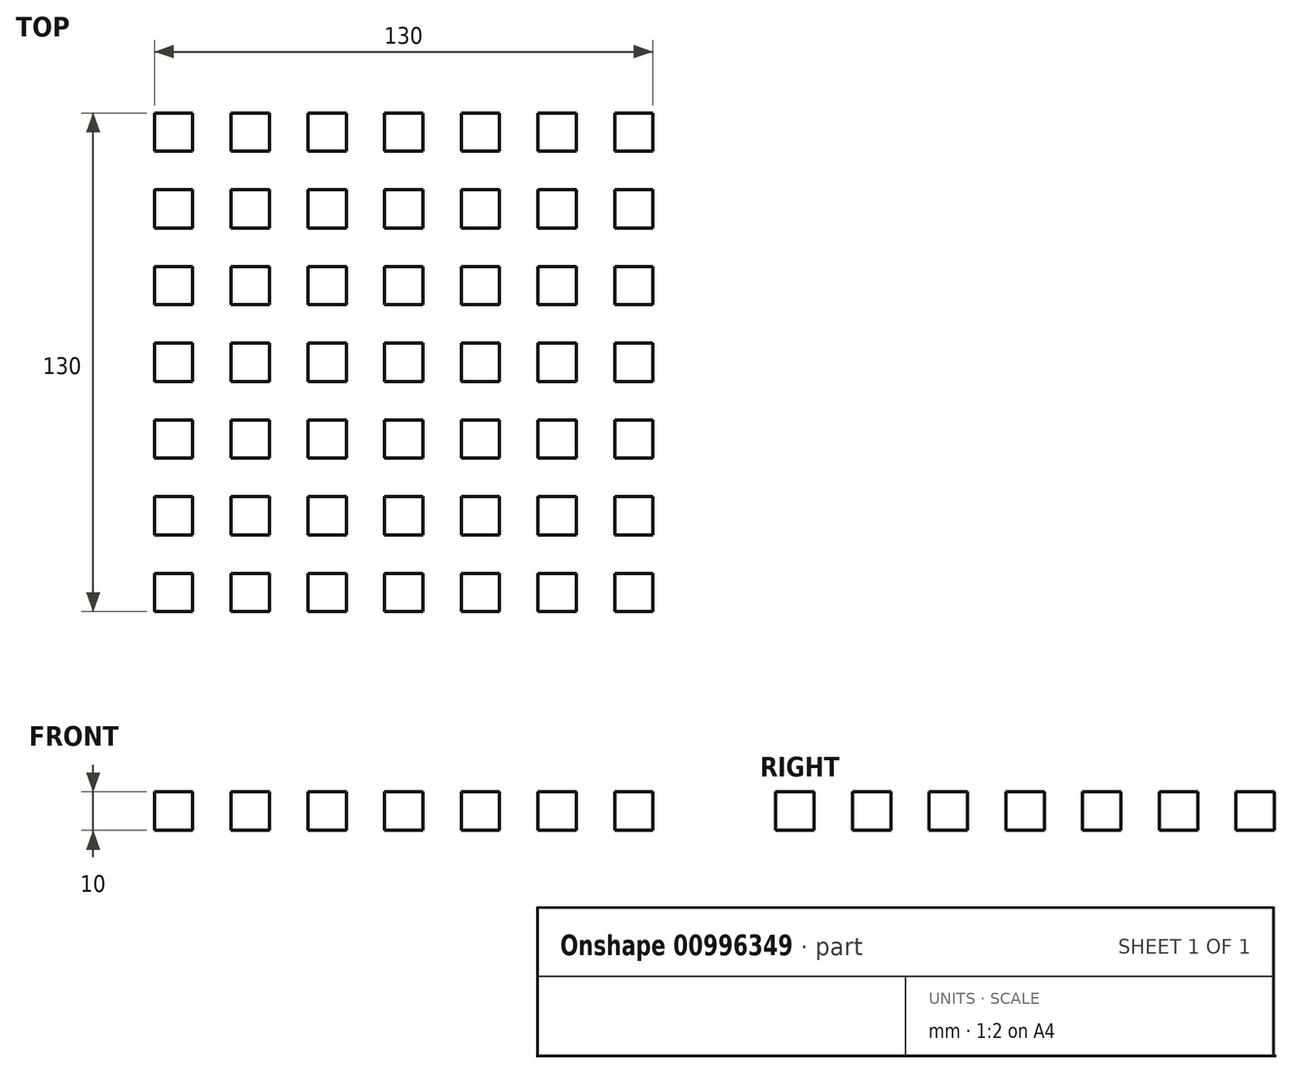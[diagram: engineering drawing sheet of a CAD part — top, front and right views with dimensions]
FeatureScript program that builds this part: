
annotation { "Feature Type Name" : "Feature", "Feature Type Description" : "" }
export const myFeature = defineFeature(function(context is Context, id is Id, definition is map)
    precondition{}
    {
        {
            var Q0;
            Q0=qCreatedBy(makeId("Top.planeOp"),FACE);
            var sketch = newSketch(context, id + "F0", { "sketchPlane" : qUnion([Q0])});
            skLineSegment(sketch, "E0.bottom", {"start": v(-62.96, -56.12) * mm, "end": v(-52.96, -56.12) * mm});
            skLineSegment(sketch, "E0.top", {"start": v(-62.96, -66.12) * mm, "end": v(-52.96, -66.12) * mm});
            skLineSegment(sketch, "E0.left", {"start": v(-62.96, -56.12) * mm, "end": v(-62.96, -66.12) * mm});
            skLineSegment(sketch, "E0.right", {"start": v(-52.96, -56.12) * mm, "end": v(-52.96, -66.12) * mm});
            skLineSegment(sketch, "E1.0.1.0", {"start": v(-62.96, -36.12) * mm, "end": v(-62.96, -46.12) * mm});
            skLineSegment(sketch, "E1.0.1.1", {"start": v(-52.96, -36.12) * mm, "end": v(-52.96, -46.12) * mm});
            skLineSegment(sketch, "E1.0.1.2", {"start": v(-62.96, -36.12) * mm, "end": v(-52.96, -36.12) * mm});
            skLineSegment(sketch, "E1.0.1.3", {"start": v(-62.96, -46.12) * mm, "end": v(-52.96, -46.12) * mm});
            skLineSegment(sketch, "E1.0.2.0", {"start": v(-62.96, -16.12) * mm, "end": v(-62.96, -26.12) * mm});
            skLineSegment(sketch, "E1.0.2.1", {"start": v(-52.96, -16.12) * mm, "end": v(-52.96, -26.12) * mm});
            skLineSegment(sketch, "E1.0.2.2", {"start": v(-62.96, -16.12) * mm, "end": v(-52.96, -16.12) * mm});
            skLineSegment(sketch, "E1.0.2.3", {"start": v(-62.96, -26.12) * mm, "end": v(-52.96, -26.12) * mm});
            skLineSegment(sketch, "E1.0.3.0", {"start": v(-62.96, 3.88) * mm, "end": v(-62.96, -6.12) * mm});
            skLineSegment(sketch, "E1.0.3.1", {"start": v(-52.96, 3.88) * mm, "end": v(-52.96, -6.12) * mm});
            skLineSegment(sketch, "E1.0.3.2", {"start": v(-62.96, 3.88) * mm, "end": v(-52.96, 3.88) * mm});
            skLineSegment(sketch, "E1.0.3.3", {"start": v(-62.96, -6.12) * mm, "end": v(-52.96, -6.12) * mm});
            skLineSegment(sketch, "E1.0.4.0", {"start": v(-62.96, 23.88) * mm, "end": v(-62.96, 13.88) * mm});
            skLineSegment(sketch, "E1.0.4.1", {"start": v(-52.96, 23.88) * mm, "end": v(-52.96, 13.88) * mm});
            skLineSegment(sketch, "E1.0.4.2", {"start": v(-62.96, 23.88) * mm, "end": v(-52.96, 23.88) * mm});
            skLineSegment(sketch, "E1.0.4.3", {"start": v(-62.96, 13.88) * mm, "end": v(-52.96, 13.88) * mm});
            skLineSegment(sketch, "E1.1.0.0", {"start": v(-42.96, -56.12) * mm, "end": v(-42.96, -66.12) * mm});
            skLineSegment(sketch, "E1.1.0.1", {"start": v(-32.96, -56.12) * mm, "end": v(-32.96, -66.12) * mm});
            skLineSegment(sketch, "E1.1.0.2", {"start": v(-42.96, -56.12) * mm, "end": v(-32.96, -56.12) * mm});
            skLineSegment(sketch, "E1.1.0.3", {"start": v(-42.96, -66.12) * mm, "end": v(-32.96, -66.12) * mm});
            skLineSegment(sketch, "E1.1.1.0", {"start": v(-42.96, -36.12) * mm, "end": v(-42.96, -46.12) * mm});
            skLineSegment(sketch, "E1.1.1.1", {"start": v(-32.96, -36.12) * mm, "end": v(-32.96, -46.12) * mm});
            skLineSegment(sketch, "E1.1.1.2", {"start": v(-42.96, -36.12) * mm, "end": v(-32.96, -36.12) * mm});
            skLineSegment(sketch, "E1.1.1.3", {"start": v(-42.96, -46.12) * mm, "end": v(-32.96, -46.12) * mm});
            skLineSegment(sketch, "E1.1.2.0", {"start": v(-42.96, -16.12) * mm, "end": v(-42.96, -26.12) * mm});
            skLineSegment(sketch, "E1.1.2.1", {"start": v(-32.96, -16.12) * mm, "end": v(-32.96, -26.12) * mm});
            skLineSegment(sketch, "E1.1.2.2", {"start": v(-42.96, -16.12) * mm, "end": v(-32.96, -16.12) * mm});
            skLineSegment(sketch, "E1.1.2.3", {"start": v(-42.96, -26.12) * mm, "end": v(-32.96, -26.12) * mm});
            skLineSegment(sketch, "E1.1.3.0", {"start": v(-42.96, 3.88) * mm, "end": v(-42.96, -6.12) * mm});
            skLineSegment(sketch, "E1.1.3.1", {"start": v(-32.96, 3.88) * mm, "end": v(-32.96, -6.12) * mm});
            skLineSegment(sketch, "E1.1.3.2", {"start": v(-42.96, 3.88) * mm, "end": v(-32.96, 3.88) * mm});
            skLineSegment(sketch, "E1.1.3.3", {"start": v(-42.96, -6.12) * mm, "end": v(-32.96, -6.12) * mm});
            skLineSegment(sketch, "E1.1.4.0", {"start": v(-42.96, 23.88) * mm, "end": v(-42.96, 13.88) * mm});
            skLineSegment(sketch, "E1.1.4.1", {"start": v(-32.96, 23.88) * mm, "end": v(-32.96, 13.88) * mm});
            skLineSegment(sketch, "E1.1.4.2", {"start": v(-42.96, 23.88) * mm, "end": v(-32.96, 23.88) * mm});
            skLineSegment(sketch, "E1.1.4.3", {"start": v(-42.96, 13.88) * mm, "end": v(-32.96, 13.88) * mm});
            skLineSegment(sketch, "E1.2.0.0", {"start": v(-22.96, -56.12) * mm, "end": v(-22.96, -66.12) * mm});
            skLineSegment(sketch, "E1.2.0.1", {"start": v(-12.96, -56.12) * mm, "end": v(-12.96, -66.12) * mm});
            skLineSegment(sketch, "E1.2.0.2", {"start": v(-22.96, -56.12) * mm, "end": v(-12.96, -56.12) * mm});
            skLineSegment(sketch, "E1.2.0.3", {"start": v(-22.96, -66.12) * mm, "end": v(-12.96, -66.12) * mm});
            skLineSegment(sketch, "E1.2.1.0", {"start": v(-22.96, -36.12) * mm, "end": v(-22.96, -46.12) * mm});
            skLineSegment(sketch, "E1.2.1.1", {"start": v(-12.96, -36.12) * mm, "end": v(-12.96, -46.12) * mm});
            skLineSegment(sketch, "E1.2.1.2", {"start": v(-22.96, -36.12) * mm, "end": v(-12.96, -36.12) * mm});
            skLineSegment(sketch, "E1.2.1.3", {"start": v(-22.96, -46.12) * mm, "end": v(-12.96, -46.12) * mm});
            skLineSegment(sketch, "E1.2.2.0", {"start": v(-22.96, -16.12) * mm, "end": v(-22.96, -26.12) * mm});
            skLineSegment(sketch, "E1.2.2.1", {"start": v(-12.96, -16.12) * mm, "end": v(-12.96, -26.12) * mm});
            skLineSegment(sketch, "E1.2.2.2", {"start": v(-22.96, -16.12) * mm, "end": v(-12.96, -16.12) * mm});
            skLineSegment(sketch, "E1.2.2.3", {"start": v(-22.96, -26.12) * mm, "end": v(-12.96, -26.12) * mm});
            skLineSegment(sketch, "E1.2.3.0", {"start": v(-22.96, 3.88) * mm, "end": v(-22.96, -6.12) * mm});
            skLineSegment(sketch, "E1.2.3.1", {"start": v(-12.96, 3.88) * mm, "end": v(-12.96, -6.12) * mm});
            skLineSegment(sketch, "E1.2.3.2", {"start": v(-22.96, 3.88) * mm, "end": v(-12.96, 3.88) * mm});
            skLineSegment(sketch, "E1.2.3.3", {"start": v(-22.96, -6.12) * mm, "end": v(-12.96, -6.12) * mm});
            skLineSegment(sketch, "E1.2.4.0", {"start": v(-22.96, 23.88) * mm, "end": v(-22.96, 13.88) * mm});
            skLineSegment(sketch, "E1.2.4.1", {"start": v(-12.96, 23.88) * mm, "end": v(-12.96, 13.88) * mm});
            skLineSegment(sketch, "E1.2.4.2", {"start": v(-22.96, 23.88) * mm, "end": v(-12.96, 23.88) * mm});
            skLineSegment(sketch, "E1.2.4.3", {"start": v(-22.96, 13.88) * mm, "end": v(-12.96, 13.88) * mm});
            skLineSegment(sketch, "E1.3.0.0", {"start": v(-2.96, -56.12) * mm, "end": v(-2.96, -66.12) * mm});
            skLineSegment(sketch, "E1.3.0.1", {"start": v(7.04, -56.12) * mm, "end": v(7.04, -66.12) * mm});
            skLineSegment(sketch, "E1.3.0.2", {"start": v(-2.96, -56.12) * mm, "end": v(7.04, -56.12) * mm});
            skLineSegment(sketch, "E1.3.0.3", {"start": v(-2.96, -66.12) * mm, "end": v(7.04, -66.12) * mm});
            skLineSegment(sketch, "E1.3.1.0", {"start": v(-2.96, -36.12) * mm, "end": v(-2.96, -46.12) * mm});
            skLineSegment(sketch, "E1.3.1.1", {"start": v(7.04, -36.12) * mm, "end": v(7.04, -46.12) * mm});
            skLineSegment(sketch, "E1.3.1.2", {"start": v(-2.96, -36.12) * mm, "end": v(7.04, -36.12) * mm});
            skLineSegment(sketch, "E1.3.1.3", {"start": v(-2.96, -46.12) * mm, "end": v(7.04, -46.12) * mm});
            skLineSegment(sketch, "E1.3.2.0", {"start": v(-2.96, -16.12) * mm, "end": v(-2.96, -26.12) * mm});
            skLineSegment(sketch, "E1.3.2.1", {"start": v(7.04, -16.12) * mm, "end": v(7.04, -26.12) * mm});
            skLineSegment(sketch, "E1.3.2.2", {"start": v(-2.96, -16.12) * mm, "end": v(7.04, -16.12) * mm});
            skLineSegment(sketch, "E1.3.2.3", {"start": v(-2.96, -26.12) * mm, "end": v(7.04, -26.12) * mm});
            skLineSegment(sketch, "E1.3.3.0", {"start": v(-2.96, 3.88) * mm, "end": v(-2.96, -6.12) * mm});
            skLineSegment(sketch, "E1.3.3.1", {"start": v(7.04, 3.88) * mm, "end": v(7.04, -6.12) * mm});
            skLineSegment(sketch, "E1.3.3.2", {"start": v(-2.96, 3.88) * mm, "end": v(7.04, 3.88) * mm});
            skLineSegment(sketch, "E1.3.3.3", {"start": v(-2.96, -6.12) * mm, "end": v(7.04, -6.12) * mm});
            skLineSegment(sketch, "E1.3.4.0", {"start": v(-2.96, 23.88) * mm, "end": v(-2.96, 13.88) * mm});
            skLineSegment(sketch, "E1.3.4.1", {"start": v(7.04, 23.88) * mm, "end": v(7.04, 13.88) * mm});
            skLineSegment(sketch, "E1.3.4.2", {"start": v(-2.96, 23.88) * mm, "end": v(7.04, 23.88) * mm});
            skLineSegment(sketch, "E1.3.4.3", {"start": v(-2.96, 13.88) * mm, "end": v(7.04, 13.88) * mm});
            skLineSegment(sketch, "E1.4.0.0", {"start": v(17.04, -56.12) * mm, "end": v(17.04, -66.12) * mm});
            skLineSegment(sketch, "E1.4.0.1", {"start": v(27.04, -56.12) * mm, "end": v(27.04, -66.12) * mm});
            skLineSegment(sketch, "E1.4.0.2", {"start": v(17.04, -56.12) * mm, "end": v(27.04, -56.12) * mm});
            skLineSegment(sketch, "E1.4.0.3", {"start": v(17.04, -66.12) * mm, "end": v(27.04, -66.12) * mm});
            skLineSegment(sketch, "E1.4.1.0", {"start": v(17.04, -36.12) * mm, "end": v(17.04, -46.12) * mm});
            skLineSegment(sketch, "E1.4.1.1", {"start": v(27.04, -36.12) * mm, "end": v(27.04, -46.12) * mm});
            skLineSegment(sketch, "E1.4.1.2", {"start": v(17.04, -36.12) * mm, "end": v(27.04, -36.12) * mm});
            skLineSegment(sketch, "E1.4.1.3", {"start": v(17.04, -46.12) * mm, "end": v(27.04, -46.12) * mm});
            skLineSegment(sketch, "E1.4.2.0", {"start": v(17.04, -16.12) * mm, "end": v(17.04, -26.12) * mm});
            skLineSegment(sketch, "E1.4.2.1", {"start": v(27.04, -16.12) * mm, "end": v(27.04, -26.12) * mm});
            skLineSegment(sketch, "E1.4.2.2", {"start": v(17.04, -16.12) * mm, "end": v(27.04, -16.12) * mm});
            skLineSegment(sketch, "E1.4.2.3", {"start": v(17.04, -26.12) * mm, "end": v(27.04, -26.12) * mm});
            skLineSegment(sketch, "E1.4.3.0", {"start": v(17.04, 3.88) * mm, "end": v(17.04, -6.12) * mm});
            skLineSegment(sketch, "E1.4.3.1", {"start": v(27.04, 3.88) * mm, "end": v(27.04, -6.12) * mm});
            skLineSegment(sketch, "E1.4.3.2", {"start": v(17.04, 3.88) * mm, "end": v(27.04, 3.88) * mm});
            skLineSegment(sketch, "E1.4.3.3", {"start": v(17.04, -6.12) * mm, "end": v(27.04, -6.12) * mm});
            skLineSegment(sketch, "E1.4.4.0", {"start": v(17.04, 23.88) * mm, "end": v(17.04, 13.88) * mm});
            skLineSegment(sketch, "E1.4.4.1", {"start": v(27.04, 23.88) * mm, "end": v(27.04, 13.88) * mm});
            skLineSegment(sketch, "E1.4.4.2", {"start": v(17.04, 23.88) * mm, "end": v(27.04, 23.88) * mm});
            skLineSegment(sketch, "E1.4.4.3", {"start": v(17.04, 13.88) * mm, "end": v(27.04, 13.88) * mm});
            skLineSegment(sketch, "E1.direction1", {"start": v(-62.96, -66.12) * mm, "end": v(-42.96, -66.12) * mm, "construction": true});
            skLineSegment(sketch, "E1.direction2", {"start": v(-62.96, -66.12) * mm, "end": v(-62.96, -46.12) * mm, "construction": true});
            skLineSegment(sketch, "E2.0.0.5", {"start": v(-62.96, 43.88) * mm, "end": v(-62.96, 33.88) * mm});
            skLineSegment(sketch, "E2.3.0.5", {"start": v(-52.96, 43.88) * mm, "end": v(-52.96, 33.88) * mm});
            skLineSegment(sketch, "E2.6.0.5", {"start": v(-62.96, 43.88) * mm, "end": v(-52.96, 43.88) * mm});
            skLineSegment(sketch, "E2.9.0.5", {"start": v(-62.96, 33.88) * mm, "end": v(-52.96, 33.88) * mm});
            skLineSegment(sketch, "E2.0.0.6", {"start": v(-62.96, 63.88) * mm, "end": v(-62.96, 53.88) * mm});
            skLineSegment(sketch, "E2.3.0.6", {"start": v(-52.96, 63.88) * mm, "end": v(-52.96, 53.88) * mm});
            skLineSegment(sketch, "E2.6.0.6", {"start": v(-62.96, 63.88) * mm, "end": v(-52.96, 63.88) * mm});
            skLineSegment(sketch, "E2.9.0.6", {"start": v(-62.96, 53.88) * mm, "end": v(-52.96, 53.88) * mm});
            skLineSegment(sketch, "E2.0.1.5", {"start": v(-42.96, 43.88) * mm, "end": v(-42.96, 33.88) * mm});
            skLineSegment(sketch, "E2.3.1.5", {"start": v(-32.96, 43.88) * mm, "end": v(-32.96, 33.88) * mm});
            skLineSegment(sketch, "E2.6.1.5", {"start": v(-42.96, 43.88) * mm, "end": v(-32.96, 43.88) * mm});
            skLineSegment(sketch, "E2.9.1.5", {"start": v(-42.96, 33.88) * mm, "end": v(-32.96, 33.88) * mm});
            skLineSegment(sketch, "E2.0.1.6", {"start": v(-42.96, 63.88) * mm, "end": v(-42.96, 53.88) * mm});
            skLineSegment(sketch, "E2.3.1.6", {"start": v(-32.96, 63.88) * mm, "end": v(-32.96, 53.88) * mm});
            skLineSegment(sketch, "E2.6.1.6", {"start": v(-42.96, 63.88) * mm, "end": v(-32.96, 63.88) * mm});
            skLineSegment(sketch, "E2.9.1.6", {"start": v(-42.96, 53.88) * mm, "end": v(-32.96, 53.88) * mm});
            skLineSegment(sketch, "E2.0.2.5", {"start": v(-22.96, 43.88) * mm, "end": v(-22.96, 33.88) * mm});
            skLineSegment(sketch, "E2.3.2.5", {"start": v(-12.96, 43.88) * mm, "end": v(-12.96, 33.88) * mm});
            skLineSegment(sketch, "E2.6.2.5", {"start": v(-22.96, 43.88) * mm, "end": v(-12.96, 43.88) * mm});
            skLineSegment(sketch, "E2.9.2.5", {"start": v(-22.96, 33.88) * mm, "end": v(-12.96, 33.88) * mm});
            skLineSegment(sketch, "E2.0.2.6", {"start": v(-22.96, 63.88) * mm, "end": v(-22.96, 53.88) * mm});
            skLineSegment(sketch, "E2.3.2.6", {"start": v(-12.96, 63.88) * mm, "end": v(-12.96, 53.88) * mm});
            skLineSegment(sketch, "E2.6.2.6", {"start": v(-22.96, 63.88) * mm, "end": v(-12.96, 63.88) * mm});
            skLineSegment(sketch, "E2.9.2.6", {"start": v(-22.96, 53.88) * mm, "end": v(-12.96, 53.88) * mm});
            skLineSegment(sketch, "E2.0.3.5", {"start": v(-2.96, 43.88) * mm, "end": v(-2.96, 33.88) * mm});
            skLineSegment(sketch, "E2.3.3.5", {"start": v(7.04, 43.88) * mm, "end": v(7.04, 33.88) * mm});
            skLineSegment(sketch, "E2.6.3.5", {"start": v(-2.96, 43.88) * mm, "end": v(7.04, 43.88) * mm});
            skLineSegment(sketch, "E2.9.3.5", {"start": v(-2.96, 33.88) * mm, "end": v(7.04, 33.88) * mm});
            skLineSegment(sketch, "E2.0.3.6", {"start": v(-2.96, 63.88) * mm, "end": v(-2.96, 53.88) * mm});
            skLineSegment(sketch, "E2.3.3.6", {"start": v(7.04, 63.88) * mm, "end": v(7.04, 53.88) * mm});
            skLineSegment(sketch, "E2.6.3.6", {"start": v(-2.96, 63.88) * mm, "end": v(7.04, 63.88) * mm});
            skLineSegment(sketch, "E2.9.3.6", {"start": v(-2.96, 53.88) * mm, "end": v(7.04, 53.88) * mm});
            skLineSegment(sketch, "E2.0.4.5", {"start": v(17.04, 43.88) * mm, "end": v(17.04, 33.88) * mm});
            skLineSegment(sketch, "E2.3.4.5", {"start": v(27.04, 43.88) * mm, "end": v(27.04, 33.88) * mm});
            skLineSegment(sketch, "E2.6.4.5", {"start": v(17.04, 43.88) * mm, "end": v(27.04, 43.88) * mm});
            skLineSegment(sketch, "E2.9.4.5", {"start": v(17.04, 33.88) * mm, "end": v(27.04, 33.88) * mm});
            skLineSegment(sketch, "E2.0.4.6", {"start": v(17.04, 63.88) * mm, "end": v(17.04, 53.88) * mm});
            skLineSegment(sketch, "E2.3.4.6", {"start": v(27.04, 63.88) * mm, "end": v(27.04, 53.88) * mm});
            skLineSegment(sketch, "E2.6.4.6", {"start": v(17.04, 63.88) * mm, "end": v(27.04, 63.88) * mm});
            skLineSegment(sketch, "E2.9.4.6", {"start": v(17.04, 53.88) * mm, "end": v(27.04, 53.88) * mm});
            skLineSegment(sketch, "E3.0.5.0", {"start": v(37.04, -56.12) * mm, "end": v(37.04, -66.12) * mm});
            skLineSegment(sketch, "E3.3.5.0", {"start": v(47.04, -56.12) * mm, "end": v(47.04, -66.12) * mm});
            skLineSegment(sketch, "E3.6.5.0", {"start": v(37.04, -56.12) * mm, "end": v(47.04, -56.12) * mm});
            skLineSegment(sketch, "E3.9.5.0", {"start": v(37.04, -66.12) * mm, "end": v(47.04, -66.12) * mm});
            skLineSegment(sketch, "E3.0.5.1", {"start": v(37.04, -36.12) * mm, "end": v(37.04, -46.12) * mm});
            skLineSegment(sketch, "E3.3.5.1", {"start": v(47.04, -36.12) * mm, "end": v(47.04, -46.12) * mm});
            skLineSegment(sketch, "E3.6.5.1", {"start": v(37.04, -36.12) * mm, "end": v(47.04, -36.12) * mm});
            skLineSegment(sketch, "E3.9.5.1", {"start": v(37.04, -46.12) * mm, "end": v(47.04, -46.12) * mm});
            skLineSegment(sketch, "E3.0.5.2", {"start": v(37.04, -16.12) * mm, "end": v(37.04, -26.12) * mm});
            skLineSegment(sketch, "E3.3.5.2", {"start": v(47.04, -16.12) * mm, "end": v(47.04, -26.12) * mm});
            skLineSegment(sketch, "E3.6.5.2", {"start": v(37.04, -16.12) * mm, "end": v(47.04, -16.12) * mm});
            skLineSegment(sketch, "E3.9.5.2", {"start": v(37.04, -26.12) * mm, "end": v(47.04, -26.12) * mm});
            skLineSegment(sketch, "E3.0.5.3", {"start": v(37.04, 3.88) * mm, "end": v(37.04, -6.12) * mm});
            skLineSegment(sketch, "E3.3.5.3", {"start": v(47.04, 3.88) * mm, "end": v(47.04, -6.12) * mm});
            skLineSegment(sketch, "E3.6.5.3", {"start": v(37.04, 3.88) * mm, "end": v(47.04, 3.88) * mm});
            skLineSegment(sketch, "E3.9.5.3", {"start": v(37.04, -6.12) * mm, "end": v(47.04, -6.12) * mm});
            skLineSegment(sketch, "E3.0.5.4", {"start": v(37.04, 23.88) * mm, "end": v(37.04, 13.88) * mm});
            skLineSegment(sketch, "E3.3.5.4", {"start": v(47.04, 23.88) * mm, "end": v(47.04, 13.88) * mm});
            skLineSegment(sketch, "E3.6.5.4", {"start": v(37.04, 23.88) * mm, "end": v(47.04, 23.88) * mm});
            skLineSegment(sketch, "E3.9.5.4", {"start": v(37.04, 13.88) * mm, "end": v(47.04, 13.88) * mm});
            skLineSegment(sketch, "E3.0.5.5", {"start": v(37.04, 43.88) * mm, "end": v(37.04, 33.88) * mm});
            skLineSegment(sketch, "E3.3.5.5", {"start": v(47.04, 43.88) * mm, "end": v(47.04, 33.88) * mm});
            skLineSegment(sketch, "E3.6.5.5", {"start": v(37.04, 43.88) * mm, "end": v(47.04, 43.88) * mm});
            skLineSegment(sketch, "E3.9.5.5", {"start": v(37.04, 33.88) * mm, "end": v(47.04, 33.88) * mm});
            skLineSegment(sketch, "E3.0.5.6", {"start": v(37.04, 63.88) * mm, "end": v(37.04, 53.88) * mm});
            skLineSegment(sketch, "E3.3.5.6", {"start": v(47.04, 63.88) * mm, "end": v(47.04, 53.88) * mm});
            skLineSegment(sketch, "E3.6.5.6", {"start": v(37.04, 63.88) * mm, "end": v(47.04, 63.88) * mm});
            skLineSegment(sketch, "E3.9.5.6", {"start": v(37.04, 53.88) * mm, "end": v(47.04, 53.88) * mm});
            skLineSegment(sketch, "E3.0.6.0", {"start": v(57.04, -56.12) * mm, "end": v(57.04, -66.12) * mm});
            skLineSegment(sketch, "E3.3.6.0", {"start": v(67.04, -56.12) * mm, "end": v(67.04, -66.12) * mm});
            skLineSegment(sketch, "E3.6.6.0", {"start": v(57.04, -56.12) * mm, "end": v(67.04, -56.12) * mm});
            skLineSegment(sketch, "E3.9.6.0", {"start": v(57.04, -66.12) * mm, "end": v(67.04, -66.12) * mm});
            skLineSegment(sketch, "E3.0.6.1", {"start": v(57.04, -36.12) * mm, "end": v(57.04, -46.12) * mm});
            skLineSegment(sketch, "E3.3.6.1", {"start": v(67.04, -36.12) * mm, "end": v(67.04, -46.12) * mm});
            skLineSegment(sketch, "E3.6.6.1", {"start": v(57.04, -36.12) * mm, "end": v(67.04, -36.12) * mm});
            skLineSegment(sketch, "E3.9.6.1", {"start": v(57.04, -46.12) * mm, "end": v(67.04, -46.12) * mm});
            skLineSegment(sketch, "E3.0.6.2", {"start": v(57.04, -16.12) * mm, "end": v(57.04, -26.12) * mm});
            skLineSegment(sketch, "E3.3.6.2", {"start": v(67.04, -16.12) * mm, "end": v(67.04, -26.12) * mm});
            skLineSegment(sketch, "E3.6.6.2", {"start": v(57.04, -16.12) * mm, "end": v(67.04, -16.12) * mm});
            skLineSegment(sketch, "E3.9.6.2", {"start": v(57.04, -26.12) * mm, "end": v(67.04, -26.12) * mm});
            skLineSegment(sketch, "E3.0.6.3", {"start": v(57.04, 3.88) * mm, "end": v(57.04, -6.12) * mm});
            skLineSegment(sketch, "E3.3.6.3", {"start": v(67.04, 3.88) * mm, "end": v(67.04, -6.12) * mm});
            skLineSegment(sketch, "E3.6.6.3", {"start": v(57.04, 3.88) * mm, "end": v(67.04, 3.88) * mm});
            skLineSegment(sketch, "E3.9.6.3", {"start": v(57.04, -6.12) * mm, "end": v(67.04, -6.12) * mm});
            skLineSegment(sketch, "E3.0.6.4", {"start": v(57.04, 23.88) * mm, "end": v(57.04, 13.88) * mm});
            skLineSegment(sketch, "E3.3.6.4", {"start": v(67.04, 23.88) * mm, "end": v(67.04, 13.88) * mm});
            skLineSegment(sketch, "E3.6.6.4", {"start": v(57.04, 23.88) * mm, "end": v(67.04, 23.88) * mm});
            skLineSegment(sketch, "E3.9.6.4", {"start": v(57.04, 13.88) * mm, "end": v(67.04, 13.88) * mm});
            skLineSegment(sketch, "E3.0.6.5", {"start": v(57.04, 43.88) * mm, "end": v(57.04, 33.88) * mm});
            skLineSegment(sketch, "E3.3.6.5", {"start": v(67.04, 43.88) * mm, "end": v(67.04, 33.88) * mm});
            skLineSegment(sketch, "E3.6.6.5", {"start": v(57.04, 43.88) * mm, "end": v(67.04, 43.88) * mm});
            skLineSegment(sketch, "E3.9.6.5", {"start": v(57.04, 33.88) * mm, "end": v(67.04, 33.88) * mm});
            skLineSegment(sketch, "E3.0.6.6", {"start": v(57.04, 63.88) * mm, "end": v(57.04, 53.88) * mm});
            skLineSegment(sketch, "E3.3.6.6", {"start": v(67.04, 63.88) * mm, "end": v(67.04, 53.88) * mm});
            skLineSegment(sketch, "E3.6.6.6", {"start": v(57.04, 63.88) * mm, "end": v(67.04, 63.88) * mm});
            skLineSegment(sketch, "E3.9.6.6", {"start": v(57.04, 53.88) * mm, "end": v(67.04, 53.88) * mm});
            skSolve(sketch);
        }
        {
            var Q0;
            Q0=makeQuery(id+"F0.imprint","IMPRINT",FACE,{"disambiguationData":[TD([[makeQuery(id+"F0.imprint","IMPRINT",EDGE,{"derivedFrom":sQuery(id+"F0.wireOp",EDGE,"E1.1.3.0")}),1.0]])]});
            var Q1;
            Q1=makeQuery(id+"F0.imprint","IMPRINT",FACE,{"disambiguationData":[TD([[makeQuery(id+"F0.imprint","IMPRINT",EDGE,{"derivedFrom":sQuery(id+"F0.wireOp",EDGE,"E2.0.1.5")}),1.0]])]});
            var Q2;
            Q2=makeQuery(id+"F0.imprint","IMPRINT",FACE,{"disambiguationData":[TD([[makeQuery(id+"F0.imprint","IMPRINT",EDGE,{"derivedFrom":sQuery(id+"F0.wireOp",EDGE,"E3.0.6.0")}),1.0]])]});
            var Q3;
            Q3=makeQuery(id+"F0.imprint","IMPRINT",FACE,{"disambiguationData":[TD([[makeQuery(id+"F0.imprint","IMPRINT",EDGE,{"derivedFrom":sQuery(id+"F0.wireOp",EDGE,"E1.4.0.0")}),1.0]])]});
            var Q4;
            Q4=makeQuery(id+"F0.imprint","IMPRINT",FACE,{"disambiguationData":[TD([[makeQuery(id+"F0.imprint","IMPRINT",EDGE,{"derivedFrom":sQuery(id+"F0.wireOp",EDGE,"E3.0.6.6")}),1.0]])]});
            var Q5;
            Q5=makeQuery(id+"F0.imprint","IMPRINT",FACE,{"disambiguationData":[TD([[makeQuery(id+"F0.imprint","IMPRINT",EDGE,{"derivedFrom":sQuery(id+"F0.wireOp",EDGE,"E2.0.2.6")}),1.0]])]});
            var Q6;
            Q6=makeQuery(id+"F0.imprint","IMPRINT",FACE,{"disambiguationData":[TD([[makeQuery(id+"F0.imprint","IMPRINT",EDGE,{"derivedFrom":sQuery(id+"F0.wireOp",EDGE,"E1.4.4.0")}),1.0]])]});
            var Q7;
            Q7=makeQuery(id+"F0.imprint","IMPRINT",FACE,{"disambiguationData":[TD([[makeQuery(id+"F0.imprint","IMPRINT",EDGE,{"derivedFrom":sQuery(id+"F0.wireOp",EDGE,"E2.0.4.6")}),1.0]])]});
            var Q8;
            Q8=makeQuery(id+"F0.imprint","IMPRINT",FACE,{"disambiguationData":[TD([[makeQuery(id+"F0.imprint","IMPRINT",EDGE,{"derivedFrom":sQuery(id+"F0.wireOp",EDGE,"E1.0.2.0")}),1.0]])]});
            var Q9;
            Q9=makeQuery(id+"F0.imprint","IMPRINT",FACE,{"disambiguationData":[TD([[makeQuery(id+"F0.imprint","IMPRINT",EDGE,{"derivedFrom":sQuery(id+"F0.wireOp",EDGE,"E3.0.5.3")}),1.0]])]});
            var Q10;
            Q10=makeQuery(id+"F0.imprint","IMPRINT",FACE,{"disambiguationData":[TD([[makeQuery(id+"F0.imprint","IMPRINT",EDGE,{"derivedFrom":sQuery(id+"F0.wireOp",EDGE,"E1.4.3.0")}),1.0]])]});
            var Q11;
            Q11=makeQuery(id+"F0.imprint","IMPRINT",FACE,{"disambiguationData":[TD([[makeQuery(id+"F0.imprint","IMPRINT",EDGE,{"derivedFrom":sQuery(id+"F0.wireOp",EDGE,"E1.2.0.0")}),1.0]])]});
            var Q12;
            Q12=makeQuery(id+"F0.imprint","IMPRINT",FACE,{"disambiguationData":[TD([[makeQuery(id+"F0.imprint","IMPRINT",EDGE,{"derivedFrom":sQuery(id+"F0.wireOp",EDGE,"E3.0.6.2")}),1.0]])]});
            var Q13;
            Q13=makeQuery(id+"F0.imprint","IMPRINT",FACE,{"disambiguationData":[TD([[makeQuery(id+"F0.imprint","IMPRINT",EDGE,{"derivedFrom":sQuery(id+"F0.wireOp",EDGE,"E1.3.1.0")}),1.0]])]});
            var Q14;
            Q14=makeQuery(id+"F0.imprint","IMPRINT",FACE,{"disambiguationData":[TD([[makeQuery(id+"F0.imprint","IMPRINT",EDGE,{"derivedFrom":sQuery(id+"F0.wireOp",EDGE,"E2.0.0.6")}),1.0]])]});
            var Q15;
            Q15=makeQuery(id+"F0.imprint","IMPRINT",FACE,{"disambiguationData":[TD([[makeQuery(id+"F0.imprint","IMPRINT",EDGE,{"derivedFrom":sQuery(id+"F0.wireOp",EDGE,"E2.0.1.6")}),1.0]])]});
            var Q16;
            Q16=makeQuery(id+"F0.imprint","IMPRINT",FACE,{"disambiguationData":[TD([[makeQuery(id+"F0.imprint","IMPRINT",EDGE,{"derivedFrom":sQuery(id+"F0.wireOp",EDGE,"E2.0.3.5")}),1.0]])]});
            var Q17;
            Q17=makeQuery(id+"F0.imprint","IMPRINT",FACE,{"disambiguationData":[TD([[makeQuery(id+"F0.imprint","IMPRINT",EDGE,{"derivedFrom":sQuery(id+"F0.wireOp",EDGE,"E2.0.3.6")}),1.0]])]});
            var Q18;
            Q18=makeQuery(id+"F0.imprint","IMPRINT",FACE,{"disambiguationData":[TD([[makeQuery(id+"F0.imprint","IMPRINT",EDGE,{"derivedFrom":sQuery(id+"F0.wireOp",EDGE,"E1.1.0.0")}),1.0]])]});
            var Q19;
            Q19=makeQuery(id+"F0.imprint","IMPRINT",FACE,{"disambiguationData":[TD([[makeQuery(id+"F0.imprint","IMPRINT",EDGE,{"derivedFrom":sQuery(id+"F0.wireOp",EDGE,"E3.0.6.4")}),1.0]])]});
            var Q20;
            Q20=makeQuery(id+"F0.imprint","IMPRINT",FACE,{"disambiguationData":[TD([[makeQuery(id+"F0.imprint","IMPRINT",EDGE,{"derivedFrom":sQuery(id+"F0.wireOp",EDGE,"E3.0.6.5")}),1.0]])]});
            var Q21;
            Q21=makeQuery(id+"F0.imprint","IMPRINT",FACE,{"disambiguationData":[TD([[makeQuery(id+"F0.imprint","IMPRINT",EDGE,{"derivedFrom":sQuery(id+"F0.wireOp",EDGE,"E0.bottom")}),-1.0]])]});
            var Q22;
            Q22=makeQuery(id+"F0.imprint","IMPRINT",FACE,{"disambiguationData":[TD([[makeQuery(id+"F0.imprint","IMPRINT",EDGE,{"derivedFrom":sQuery(id+"F0.wireOp",EDGE,"E1.0.3.0")}),1.0]])]});
            var Q23;
            Q23=makeQuery(id+"F0.imprint","IMPRINT",FACE,{"disambiguationData":[TD([[makeQuery(id+"F0.imprint","IMPRINT",EDGE,{"derivedFrom":sQuery(id+"F0.wireOp",EDGE,"E3.0.5.6")}),1.0]])]});
            var Q24;
            Q24=makeQuery(id+"F0.imprint","IMPRINT",FACE,{"disambiguationData":[TD([[makeQuery(id+"F0.imprint","IMPRINT",EDGE,{"derivedFrom":sQuery(id+"F0.wireOp",EDGE,"E3.0.5.5")}),1.0]])]});
            var Q25;
            Q25=makeQuery(id+"F0.imprint","IMPRINT",FACE,{"disambiguationData":[TD([[makeQuery(id+"F0.imprint","IMPRINT",EDGE,{"derivedFrom":sQuery(id+"F0.wireOp",EDGE,"E1.4.1.0")}),1.0]])]});
            var Q26;
            Q26=makeQuery(id+"F0.imprint","IMPRINT",FACE,{"disambiguationData":[TD([[makeQuery(id+"F0.imprint","IMPRINT",EDGE,{"derivedFrom":sQuery(id+"F0.wireOp",EDGE,"E3.0.6.1")}),1.0]])]});
            var Q27;
            Q27=makeQuery(id+"F0.imprint","IMPRINT",FACE,{"disambiguationData":[TD([[makeQuery(id+"F0.imprint","IMPRINT",EDGE,{"derivedFrom":sQuery(id+"F0.wireOp",EDGE,"E1.2.3.0")}),1.0]])]});
            var Q28;
            Q28=makeQuery(id+"F0.imprint","IMPRINT",FACE,{"disambiguationData":[TD([[makeQuery(id+"F0.imprint","IMPRINT",EDGE,{"derivedFrom":sQuery(id+"F0.wireOp",EDGE,"E3.0.5.2")}),1.0]])]});
            var Q29;
            Q29=makeQuery(id+"F0.imprint","IMPRINT",FACE,{"disambiguationData":[TD([[makeQuery(id+"F0.imprint","IMPRINT",EDGE,{"derivedFrom":sQuery(id+"F0.wireOp",EDGE,"E1.3.4.0")}),1.0]])]});
            var Q30;
            Q30=makeQuery(id+"F0.imprint","IMPRINT",FACE,{"disambiguationData":[TD([[makeQuery(id+"F0.imprint","IMPRINT",EDGE,{"derivedFrom":sQuery(id+"F0.wireOp",EDGE,"E1.0.1.0")}),1.0]])]});
            var Q31;
            Q31=makeQuery(id+"F0.imprint","IMPRINT",FACE,{"disambiguationData":[TD([[makeQuery(id+"F0.imprint","IMPRINT",EDGE,{"derivedFrom":sQuery(id+"F0.wireOp",EDGE,"E3.0.5.4")}),1.0]])]});
            var Q32;
            Q32=makeQuery(id+"F0.imprint","IMPRINT",FACE,{"disambiguationData":[TD([[makeQuery(id+"F0.imprint","IMPRINT",EDGE,{"derivedFrom":sQuery(id+"F0.wireOp",EDGE,"E1.1.2.0")}),1.0]])]});
            var Q33;
            Q33=makeQuery(id+"F0.imprint","IMPRINT",FACE,{"disambiguationData":[TD([[makeQuery(id+"F0.imprint","IMPRINT",EDGE,{"derivedFrom":sQuery(id+"F0.wireOp",EDGE,"E1.2.4.0")}),1.0]])]});
            var Q34;
            Q34=makeQuery(id+"F0.imprint","IMPRINT",FACE,{"disambiguationData":[TD([[makeQuery(id+"F0.imprint","IMPRINT",EDGE,{"derivedFrom":sQuery(id+"F0.wireOp",EDGE,"E1.2.2.0")}),1.0]])]});
            var Q35;
            Q35=makeQuery(id+"F0.imprint","IMPRINT",FACE,{"disambiguationData":[TD([[makeQuery(id+"F0.imprint","IMPRINT",EDGE,{"derivedFrom":sQuery(id+"F0.wireOp",EDGE,"E1.1.4.0")}),1.0]])]});
            var Q36;
            Q36=makeQuery(id+"F0.imprint","IMPRINT",FACE,{"disambiguationData":[TD([[makeQuery(id+"F0.imprint","IMPRINT",EDGE,{"derivedFrom":sQuery(id+"F0.wireOp",EDGE,"E1.2.1.0")}),1.0]])]});
            var Q37;
            Q37=makeQuery(id+"F0.imprint","IMPRINT",FACE,{"disambiguationData":[TD([[makeQuery(id+"F0.imprint","IMPRINT",EDGE,{"derivedFrom":sQuery(id+"F0.wireOp",EDGE,"E2.0.4.5")}),1.0]])]});
            var Q38;
            Q38=makeQuery(id+"F0.imprint","IMPRINT",FACE,{"disambiguationData":[TD([[makeQuery(id+"F0.imprint","IMPRINT",EDGE,{"derivedFrom":sQuery(id+"F0.wireOp",EDGE,"E1.3.0.0")}),1.0]])]});
            var Q39;
            Q39=makeQuery(id+"F0.imprint","IMPRINT",FACE,{"disambiguationData":[TD([[makeQuery(id+"F0.imprint","IMPRINT",EDGE,{"derivedFrom":sQuery(id+"F0.wireOp",EDGE,"E1.3.2.0")}),1.0]])]});
            var Q40;
            Q40=makeQuery(id+"F0.imprint","IMPRINT",FACE,{"disambiguationData":[TD([[makeQuery(id+"F0.imprint","IMPRINT",EDGE,{"derivedFrom":sQuery(id+"F0.wireOp",EDGE,"E1.1.1.0")}),1.0]])]});
            var Q41;
            Q41=makeQuery(id+"F0.imprint","IMPRINT",FACE,{"disambiguationData":[TD([[makeQuery(id+"F0.imprint","IMPRINT",EDGE,{"derivedFrom":sQuery(id+"F0.wireOp",EDGE,"E2.0.2.5")}),1.0]])]});
            var Q42;
            Q42=makeQuery(id+"F0.imprint","IMPRINT",FACE,{"disambiguationData":[TD([[makeQuery(id+"F0.imprint","IMPRINT",EDGE,{"derivedFrom":sQuery(id+"F0.wireOp",EDGE,"E1.4.2.0")}),1.0]])]});
            var Q43;
            Q43=makeQuery(id+"F0.imprint","IMPRINT",FACE,{"disambiguationData":[TD([[makeQuery(id+"F0.imprint","IMPRINT",EDGE,{"derivedFrom":sQuery(id+"F0.wireOp",EDGE,"E3.0.5.0")}),1.0]])]});
            var Q44;
            Q44=makeQuery(id+"F0.imprint","IMPRINT",FACE,{"disambiguationData":[TD([[makeQuery(id+"F0.imprint","IMPRINT",EDGE,{"derivedFrom":sQuery(id+"F0.wireOp",EDGE,"E1.0.4.0")}),1.0]])]});
            var Q45;
            Q45=makeQuery(id+"F0.imprint","IMPRINT",FACE,{"disambiguationData":[TD([[makeQuery(id+"F0.imprint","IMPRINT",EDGE,{"derivedFrom":sQuery(id+"F0.wireOp",EDGE,"E3.0.6.3")}),1.0]])]});
            var Q46;
            Q46=makeQuery(id+"F0.imprint","IMPRINT",FACE,{"disambiguationData":[TD([[makeQuery(id+"F0.imprint","IMPRINT",EDGE,{"derivedFrom":sQuery(id+"F0.wireOp",EDGE,"E3.0.5.1")}),1.0]])]});
            var Q47;
            Q47=makeQuery(id+"F0.imprint","IMPRINT",FACE,{"disambiguationData":[TD([[makeQuery(id+"F0.imprint","IMPRINT",EDGE,{"derivedFrom":sQuery(id+"F0.wireOp",EDGE,"E1.3.3.0")}),1.0]])]});
            var Q48;
            Q48=makeQuery(id+"F0.imprint","IMPRINT",FACE,{"disambiguationData":[TD([[makeQuery(id+"F0.imprint","IMPRINT",EDGE,{"derivedFrom":sQuery(id+"F0.wireOp",EDGE,"E2.0.0.5")}),1.0]])]});
            extrude(context, id + "F1", {"entities" : qUnion([Q0, Q1, Q2, Q3, Q4, Q5, Q6, Q7, Q8, Q9, Q10, Q11, Q12, Q13, Q14, Q15, Q16, Q17, Q18, Q19, Q20, Q21, Q22, Q23, Q24, Q25, Q26, Q27, Q28, Q29, Q30, Q31, Q32, Q33, Q34, Q35, Q36, Q37, Q38, Q39, Q40, Q41, Q42, Q43, Q44, Q45, Q46, Q47, Q48]), "depth" : 10 * mm, "offsetDistance" : 25 * mm});
        }
    });
